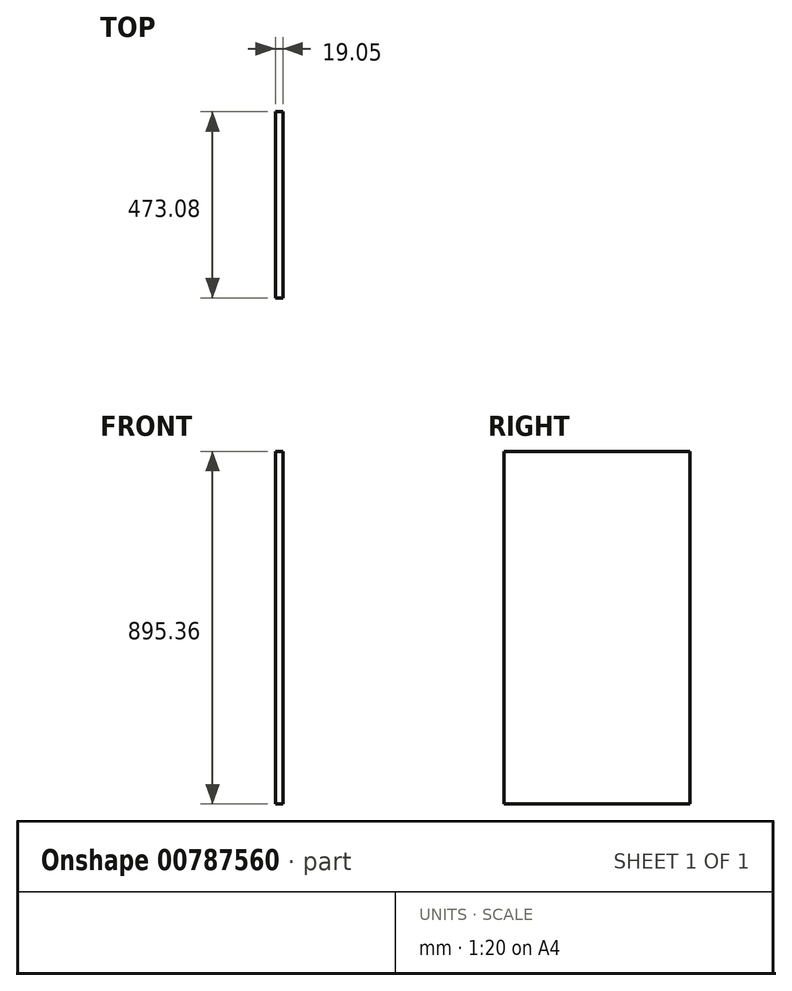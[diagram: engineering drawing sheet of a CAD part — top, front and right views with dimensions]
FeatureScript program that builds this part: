
annotation { "Feature Type Name" : "Feature", "Feature Type Description" : "" }
export const myFeature = defineFeature(function(context is Context, id is Id, definition is map)
    precondition{}
    {
        {
            var Q0;
            Q0=qCreatedBy(makeId("Right.planeOp"),FACE);
            var sketch = newSketch(context, id + "F0", { "sketchPlane" : qUnion([Q0])});
            skLineSegment(sketch, "E0.bottom", {"start": v(236.54, -447.68) * mm, "end": v(-236.54, -447.68) * mm});
            skLineSegment(sketch, "E0.top", {"start": v(236.54, 447.68) * mm, "end": v(-236.54, 447.68) * mm});
            skLineSegment(sketch, "E0.left", {"start": v(236.54, -447.68) * mm, "end": v(236.54, 447.68) * mm});
            skLineSegment(sketch, "E0.right", {"start": v(-236.54, -447.68) * mm, "end": v(-236.54, 447.68) * mm});
            skPoint(sketch, "E0.middle", {"position": v(0, 0) * mm});
            skSolve(sketch);
        }
        {
            var Q0;
            Q0 = qSketchRegion(id + "F0", true);
            extrude(context, id + "F1", {"entities" : qUnion([Q0]), "depth" : 19.05 * mm, "offsetDistance" : 25.4 * mm});
        }
    });
